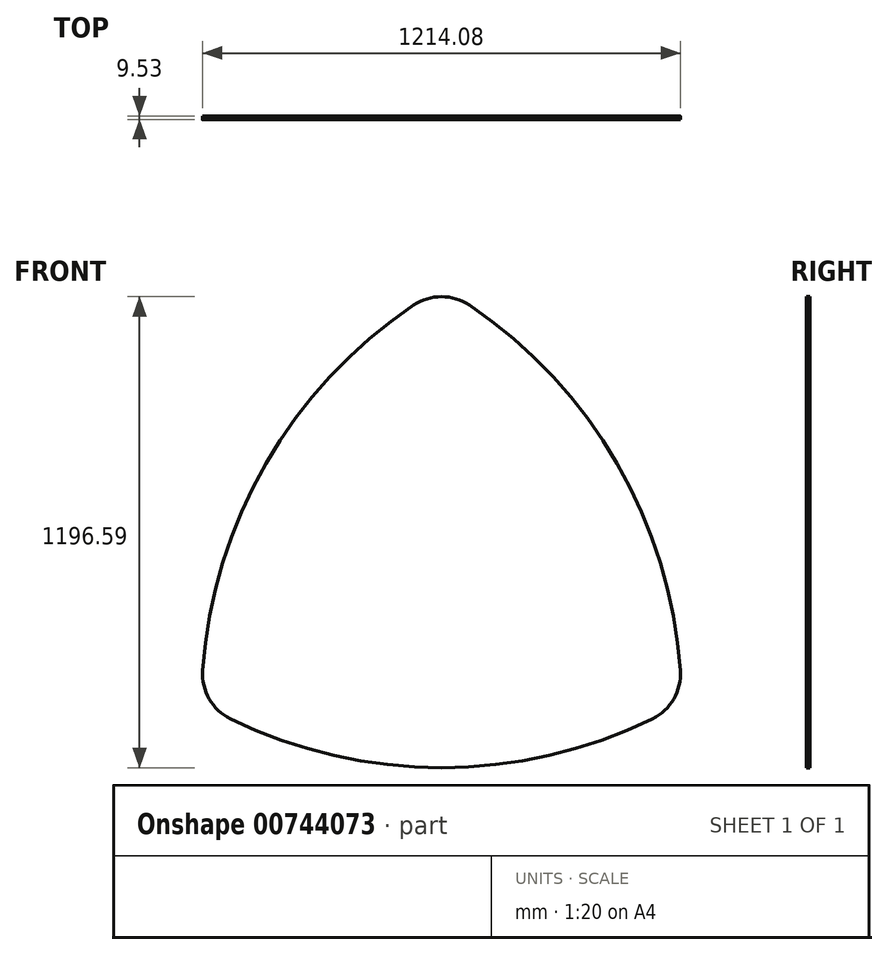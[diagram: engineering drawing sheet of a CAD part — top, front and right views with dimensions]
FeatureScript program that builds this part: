
annotation { "Feature Type Name" : "Feature", "Feature Type Description" : "" }
export const myFeature = defineFeature(function(context is Context, id is Id, definition is map)
    precondition{}
    {
        {
            var Q0;
            Q0=qCreatedBy(makeId("Front.planeOp"),FACE);
            var sketch = newSketch(context, id + "F0", { "sketchPlane" : qUnion([Q0])});
            skLineSegment(sketch, "E0", {"start": v(0, 1055.86) * mm, "end": v(-609.6, 0) * mm, "construction": true});
            skLineSegment(sketch, "E1", {"start": v(-609.6, 0) * mm, "end": v(609.6, 0) * mm, "construction": true});
            skLineSegment(sketch, "E2", {"start": v(609.6, 0) * mm, "end": v(0, 1055.86) * mm, "construction": true});
            skArc(sketch, "E3", {"start": v(609.6, 0) * mm, "mid": v(446.26, 609.6) * mm, "end": v(0, 1055.86) * mm});
            skArc(sketch, "E4", {"start": v(0, 1055.86) * mm, "mid": v(-446.26, 609.6) * mm, "end": v(-609.6, 0) * mm});
            skArc(sketch, "E5", {"start": v(-609.6, 0) * mm, "mid": v(0, -163.34) * mm, "end": v(609.6, 0) * mm});
            skSolve(sketch);
        }
        {
            var Q0;
            Q0 = qSketchRegion(id + "F0", true);
            extrude(context, id + "F1", {"entities" : qUnion([Q0]), "depth" : 9.52 * mm, "offsetDistance" : 25.4 * mm});
        }
        {
            var Q0;
            Q0=makeQuery(id+"F1.opExtrude","SWEPT_EDGE",EDGE,{"disambiguationData":[OSD([sQuery(id+"F0.wireOp",EDGE,"E3"),sQuery(id+"F0.wireOp",EDGE,"E4")])]});
            var Q1;
            Q1=makeQuery(id+"F1.opExtrude","SWEPT_EDGE",EDGE,{"disambiguationData":[OSD([sQuery(id+"F0.wireOp",EDGE,"E4"),sQuery(id+"F0.wireOp",EDGE,"BninPZxF-AQrq-mzya-6gNj-LhT5nWbNLUVP")])]});
            var Q2;
            Q2=makeQuery(id+"F1.opExtrude","SWEPT_EDGE",EDGE,{"disambiguationData":[OSD([sQuery(id+"F0.wireOp",EDGE,"E3"),sQuery(id+"F0.wireOp",EDGE,"BninPZxF-AQrq-mzya-6gNj-LhT5nWbNLUVP")])]});
            fillet(context, id + "F2", {"entities" : qUnion([Q0, Q1, Q2]), "radius" : 127 * mm, "tangentPropagation" : true, "allowEdgeOverflow" : false});
        }
    });
